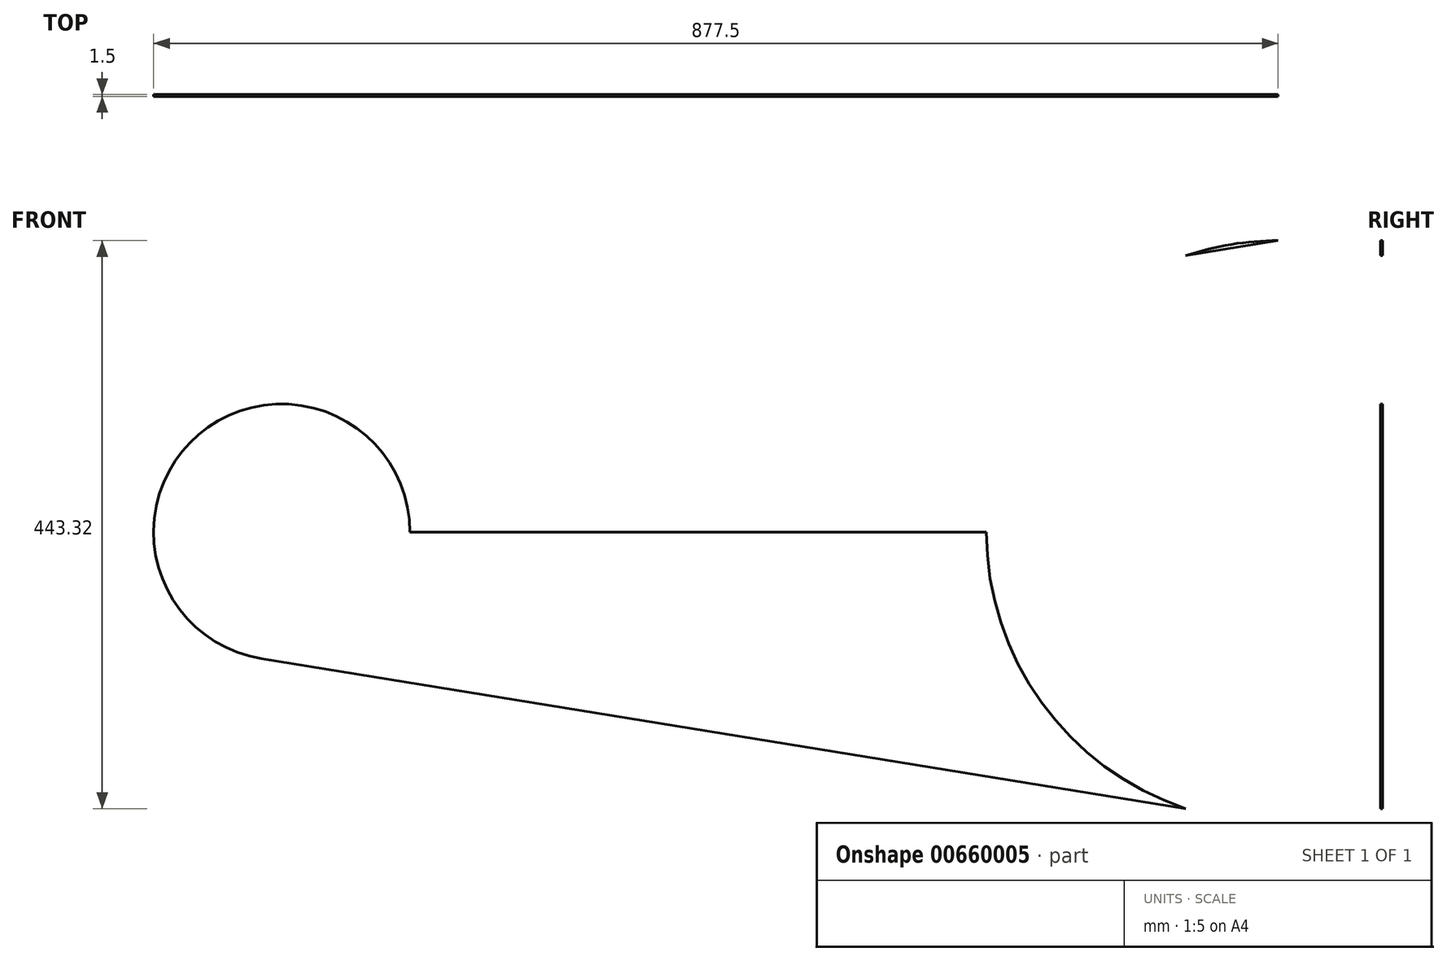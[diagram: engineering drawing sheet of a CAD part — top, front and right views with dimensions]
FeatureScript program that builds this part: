
annotation { "Feature Type Name" : "Feature", "Feature Type Description" : "" }
export const myFeature = defineFeature(function(context is Context, id is Id, definition is map)
    precondition{}
    {
        {
            var Q0;
            Q0=qCreatedBy(makeId("Front.planeOp"),FACE);
            var sketch = newSketch(context, id + "F0", { "sketchPlane" : qUnion([Q0])});
            skCircle(sketch, "E0", {"center": v(0, 0) * mm, "radius": 227.5 * mm});
            skCircle(sketch, "E1", {"center": v(-777.5, 0) * mm, "radius": 100 * mm});
            skLineSegment(sketch, "E2", {"start": v(0, 0) * mm, "end": v(-910.58, 0) * mm});
            skLineSegment(sketch, "E3", {"start": v(0, 227.5) * mm, "end": v(-793.52, 98.7) * mm});
            skLineSegment(sketch, "E4", {"start": v(0, -227.5) * mm, "end": v(-793.52, -98.7) * mm});
            skSolve(sketch);
        }
        {
            var Q0;
            {var subQ0=sQuery(id+"F0.wireOp",EDGE,"E2");var subQ1=sQuery(id+"F0.wireOp",EDGE,"E0");var subQ2=makeQuery(id+"F0.imprint","INTERSECT",VERTEX,{"derivedFrom":[subQ1,subQ0]});Q0=makeQuery(id+"F0.imprint","IMPRINT",FACE,{"disambiguationData":[TD([[makeQuery(id+"F0.imprint","IMPRINT",EDGE,{"disambiguationData":[TD([[subQ2,-1.0]])],"derivedFrom":subQ1}),-1.0]])]});}
            var Q1;
            {var subQ0=sQuery(id+"F0.wireOp",EDGE,"E3");var subQ1=sQuery(id+"F0.wireOp",EDGE,"E0");var subQ7=makeQuery(id+"F0.imprint","INTERSECT",VERTEX,{"disambiguationData":[OD(1.0)],"derivedFrom":[subQ1,subQ0]});Q1=makeQuery(id+"F0.imprint","IMPRINT",FACE,{"disambiguationData":[TD([[makeQuery(id+"F0.imprint","IMPRINT",EDGE,{"disambiguationData":[TD([[subQ7,-1.0]])],"derivedFrom":subQ1}),1.0]])]});}
            var Q2;
            {var subQ0=sQuery(id+"F0.wireOp",EDGE,"E3");var subQ1=sQuery(id+"F0.wireOp",EDGE,"E0");var subQ2=makeQuery(id+"F0.imprint","INTERSECT",VERTEX,{"disambiguationData":[OD(1.0)],"derivedFrom":[subQ1,subQ0]});Q2=makeQuery(id+"F0.imprint","IMPRINT",FACE,{"disambiguationData":[TD([[makeQuery(id+"F0.imprint","IMPRINT",EDGE,{"disambiguationData":[TD([[subQ2,-1.0]])],"derivedFrom":subQ1}),-1.0]])]});}
            var Q3;
            {var subQ0=sQuery(id+"F0.wireOp",EDGE,"E1");var subQ1=makeQuery(id+"F0.imprint","INTERSECT",VERTEX,{"derivedFrom":[subQ0,sQuery(id+"F0.wireOp",EDGE,"E4")]});Q3=makeQuery(id+"F0.imprint","IMPRINT",FACE,{"disambiguationData":[TD([[makeQuery(id+"F0.imprint","IMPRINT",EDGE,{"disambiguationData":[TD([[subQ1,1.0]])],"derivedFrom":subQ0}),1.0]])]});}
            var Q4;
            {var subQ0=sQuery(id+"F0.wireOp",EDGE,"E1");var subQ1=makeQuery(id+"F0.imprint","INTERSECT",VERTEX,{"derivedFrom":[subQ0,sQuery(id+"F0.wireOp",EDGE,"E3")]});Q4=makeQuery(id+"F0.imprint","IMPRINT",FACE,{"disambiguationData":[TD([[makeQuery(id+"F0.imprint","IMPRINT",EDGE,{"disambiguationData":[TD([[subQ1,1.0]])],"derivedFrom":subQ0}),1.0]])]});}
            extrude(context, id + "F1", {"entities" : qUnion([Q0, Q1, Q2, Q3, Q4]), "endBound" : BoundingType.SYMMETRIC, "depth" : 1.5 * mm, "offsetDistance" : 25 * mm});
        }
    });
